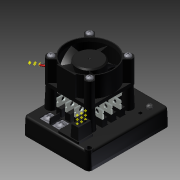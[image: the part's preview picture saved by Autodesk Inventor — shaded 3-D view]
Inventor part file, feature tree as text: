
AUTODESK INVENTOR PART (.ipt)
format: ipt  version: 2011 (Build 150239000, 239)  size: 1,472,000 bytes
history: native  units: in
note: dims shown in document units (in); Inventor stores cm internally (conversion verified against a paired STEP export)
features: other x49, plane x10, sketch x5, extrude x1
ambient origin geometry x8: Origin, YZ Plane, XZ Plane, XY Plane, X Axis, Y Axis, Z Axis, Center Point
bodies: Solid1 (feature_tree)
feature tree (65):
  other  "FR-VIC884.iam"
  other  "FR-VIC884_1.ipt:1"
  other  "FR-VIC884_2.ipt:1"
  other  "KDE1204PKBX-8.iam:1::KDE1204PKBX-8_1.ipt:1"
  other  "KDE1204PKBX-8.iam:1::KDE1204PKBX-8_2.ipt:1"
  other  "KDE1204PKBX-8.iam:1::KDE1204PKBX-8_3.ipt:1"
  other  "KDE1204PKBX-8.iam:1::KDE1204PKBX-8_4.ipt:1"
  other  "FR-VIC884_3.ipt:1"
  other  "FR-VIC884_4.ipt:1"
  other  "FR-VIC884_5.ipt:1"
  other  "FR-VIC884_6.ipt:1"
  other  "FR-VIC884_6.ipt:3"
  other  "FR-VIC884_6.ipt:4"
  other  "FR-VIC884_6.ipt:5"
  other  "FR-VIC884_6.ipt:6"
  other  "FR-VIC884_6.ipt:7"
  other  "FR-VIC884_6.ipt:8"
  other  "FR-VIC884_6.ipt:9"
  other  "FR-VIC884_6.ipt:10"
  other  "FR-VIC884_6.ipt:11"
  other  "FR-VIC884_6.ipt:12"
  other  "FR-VIC884_6.ipt:13"
  other  "FR-VIC884_7.ipt:1"
  other  "FR-VIC884_7.ipt:2"
  other  "FR-VIC884_7.ipt:3"
  other  "FR-VIC884_7.ipt:4"
  other  "Cross Recessed Fillister Head Machine Screw - Type I - Inch No. 4 - 40 - 1:1"
  other  "Cross Recessed Fillister Head Machine Screw - Type I - Inch No. 4 - 40 - 1:2"
  other  "Cross Recessed Fillister Head Machine Screw - Type I - Inch No. 4 - 40 - 1:3"
  other  "Cross Recessed Fillister Head Machine Screw - Type I - Inch No. 4 - 40 - 1:4"
  other  "FR-VIC884.iam_Bodies"
  sketch  "Sketch2"  dims[d0=0.3937in d1=1.0in d2=0.0in]
  sketch  "Sketch3"  dims[d3=0.125in]
  extrude  "Extrusion1"  Depth=1.0in TaperAngle=0.0deg
  other  "Work Point3"
  other  "Work Point4"
  other  "Work Point5"
  other  "Work Point6"
  plane  "Work Plane7"
  other  "Work Point9"
  plane  "Work Plane8"
  other  "Work Point10"
  sketch  "Sketch5"  dims[d5=0.125in]
  other  "Work Point12"
  other  "Work Point13"
  sketch  "Sketch6"  dims[d6=0.25in d7=0.125in d8=0.25in d9=0.125in d10=0.25in d11=0.125in d12=0.25in]
  other  "Work Point15"
  other  "Work Point16"
  sketch  "Sketch4"  dims[d4=0.25in]
  plane  "Work Plane1"
  other  "Work Axis1"
  plane  "Work Plane2"
  other  "Work Axis2"
  plane  "Work Plane3"
  other  "Work Axis3"
  plane  "Work Plane4"
  other  "Work Axis4"
  plane  "Work Plane9"
  other  "Work Axis6"
  plane  "Work Plane10"
  other  "Work Axis7"
  plane  "Work Plane11"
  other  "Work Axis8"
  plane  "Work Plane12"
  other  "Work Axis9"
